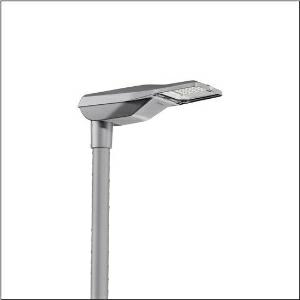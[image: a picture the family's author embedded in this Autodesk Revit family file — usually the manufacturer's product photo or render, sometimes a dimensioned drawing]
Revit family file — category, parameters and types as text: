
# Revit family: streetlight_sl_21_iq_micro___st1_5a_5xe1p31g08db_6e7e
name_source: partatom
category: Lighting Fixtures
units: mm (PartAtom-declared; Revit-internal decimal feet)

## family parameters
Cut with Voids When Loaded = No
Host = Face
Light Source = No
Part Type = Normal
Room Calculation Point = No
Round Connector Dimension = Use Diameter
Shared = No

## types (1)
- --- (1 x LED, 4730 lm, 36.4 W, 3000K)
    Apparent Load = 36 VA
    CIE Flux Codes = 22 53 95 100 100
    Color Rendering = 70
    Color Temperature = 3000K
    Default Elevation = 1800 mm
    Description = Streetlight SL 21 iQ micro, mast luminaire, primary light control with lens, of PMMA, primary optical cover: cover, of toughened safety glass, transparent, light distribution: ST1.5a, light emission: direct distribution, primary light characteristic: asymmetric, installation type: post-top, side-entry, LED, High Power LED, rated luminous flux: 4.730lm, luminous efficacy: 130lm/W, light colour: 730, colour temperature: 3000K, control gear: iQ Street-Remote, control: Street-Remote, Auto-Match, Temp-Guard, Lumen-Switch, Night-Set, Smart-Wire, Light-Fading, Desk-Remote (wireless, voltage-free reading and setting of iQ features in the workshop via application-optimized NFC function/RFID function), optimised constant luminous flux control (CLO 2.0), pre-setting: linear dimming characteristic, mains connection: 220..240V, AC, 50/60Hz, start of lifetime: 36W, end of service life: 38W, reduction: 16W, luminaire housing, of diecast aluminium, powder-coated, SITECO metallic grey (DB 702S), corrosivity category C5 high according to DIN EN ISO 12944, please order mast flange separately, inclination adjustable: 0°, 5°, 10°, 15°, sealing non-destructively replaceable, multi-level sealing system, length: 528mm, width: 235mm, height: 110mm, mast flange for spigot size: 42mm (side-entry): 5XC10008XM4, 60/48mm (side-entry/post-top): 5XC10108XM2, 76/60mm (side-entry/post-top): 5XC10108XM1, protection rating (complete): IP66, insulation class (complete): insulation class II (safety insulation), certification: CE, ENEC, ENEC+, VDE, impact resistance: IK10, permissible operating ambient temperature for outdoor applications: -40..+50°C, standard-compliant lighting for roads and squares, packaging unit: 1 piece

Light Distribution: ST1.5a
    Height = 110 mm
    Lamp = 1 x LED
    Lamp Light Flux = 4730 lm
    Lamp Power = 36.4 W
    Lamp count = 1
    Length = 528 mm
    Luminous efficacy = 130 lm/W
    Manufacturer = Siteco
    ModVariant = No
    Model = 5XE1P31G08DB
    Number of Poles = 1
    OnlyDefault = Yes
    Power Factor = 1
    Product Name = Streetlight SL 21 iQ micro | ST1.5a
    Product group = mast luminaire | pylon top
    ProductGroupID = 6100
    Protection Class = Protection class II
    Protection Degree = IP 66
    RLX_Detail_Level = 1
    RLX_Emergency_Light_Flux = 0 lm
    RLX_Emergency_Type = 0
    RLX_Emergency_Type_DB = No
    RlxData = <blob elided: 103077 chars, md5=56e9a7a3>
    Socket = socket
    Standby Power = 0 W
    System Light Flux = 4730 lm
    System Power = 36 W
    Type Comments = factory setting: luminous flux: 100 % | dim-lin: 254 | 715 mA
    Type Image = l_1006881.jpg
    URL = http://relux.com
    VarID = @adj_153355
    Voltage = 0 V
    Weight = 0.00 kg
    Width = 235 mm

## geometry (parser evidence)
native form markers: Blend x4, Sweep x12
no freeform markers — native parametric forms only
